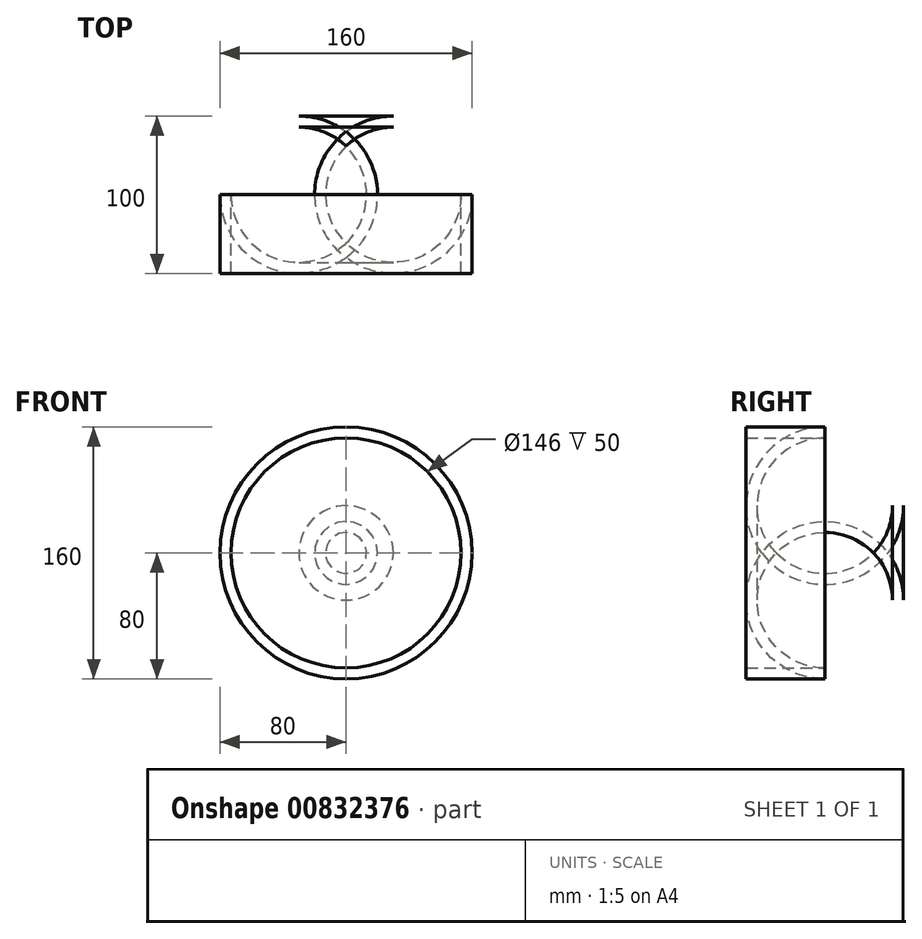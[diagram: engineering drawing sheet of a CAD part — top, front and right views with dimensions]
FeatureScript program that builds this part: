
annotation { "Feature Type Name" : "Feature", "Feature Type Description" : "" }
export const myFeature = defineFeature(function(context is Context, id is Id, definition is map)
    precondition{}
    {
        {
            var Q0;
            Q0=qCreatedBy(makeId("Front.planeOp"),FACE);
            var sketch = newSketch(context, id + "F0", { "sketchPlane" : qUnion([Q0])});
            skCircle(sketch, "E0", {"center": v(0, 0) * mm, "radius": 80 * mm});
            skSolve(sketch);
        }
        {
            var Q0;
            Q0 = qSketchRegion(id + "F0", true);
            extrude(context, id + "F1", {"entities" : qUnion([Q0]), "depth" : 100 * mm, "offsetDistance" : 25 * mm});
        }
        {
            var Q0;
            Q0=makeQuery(id+"F1.opExtrude","CAP_FACE",FACE,{"disambiguationData":[OSD([sQuery(id+"F0.wireOp",EDGE,"E0")])],"isStart":true});
            fillet(context, id + "F2", {"entities" : qUnion([Q0]), "radius" : 50 * mm, "tangentPropagation" : true, "allowEdgeOverflow" : false});
        }
        {
            var Q0;
            Q0=makeQuery(id+"F1.opExtrude","CAP_FACE",FACE,{"disambiguationData":[OSD([sQuery(id+"F0.wireOp",EDGE,"E0")])],"isStart":false});
            shell(context, id + "F3", {"entities" : qUnion([Q0]), "thickness" : 7 * mm});
        }
    });
